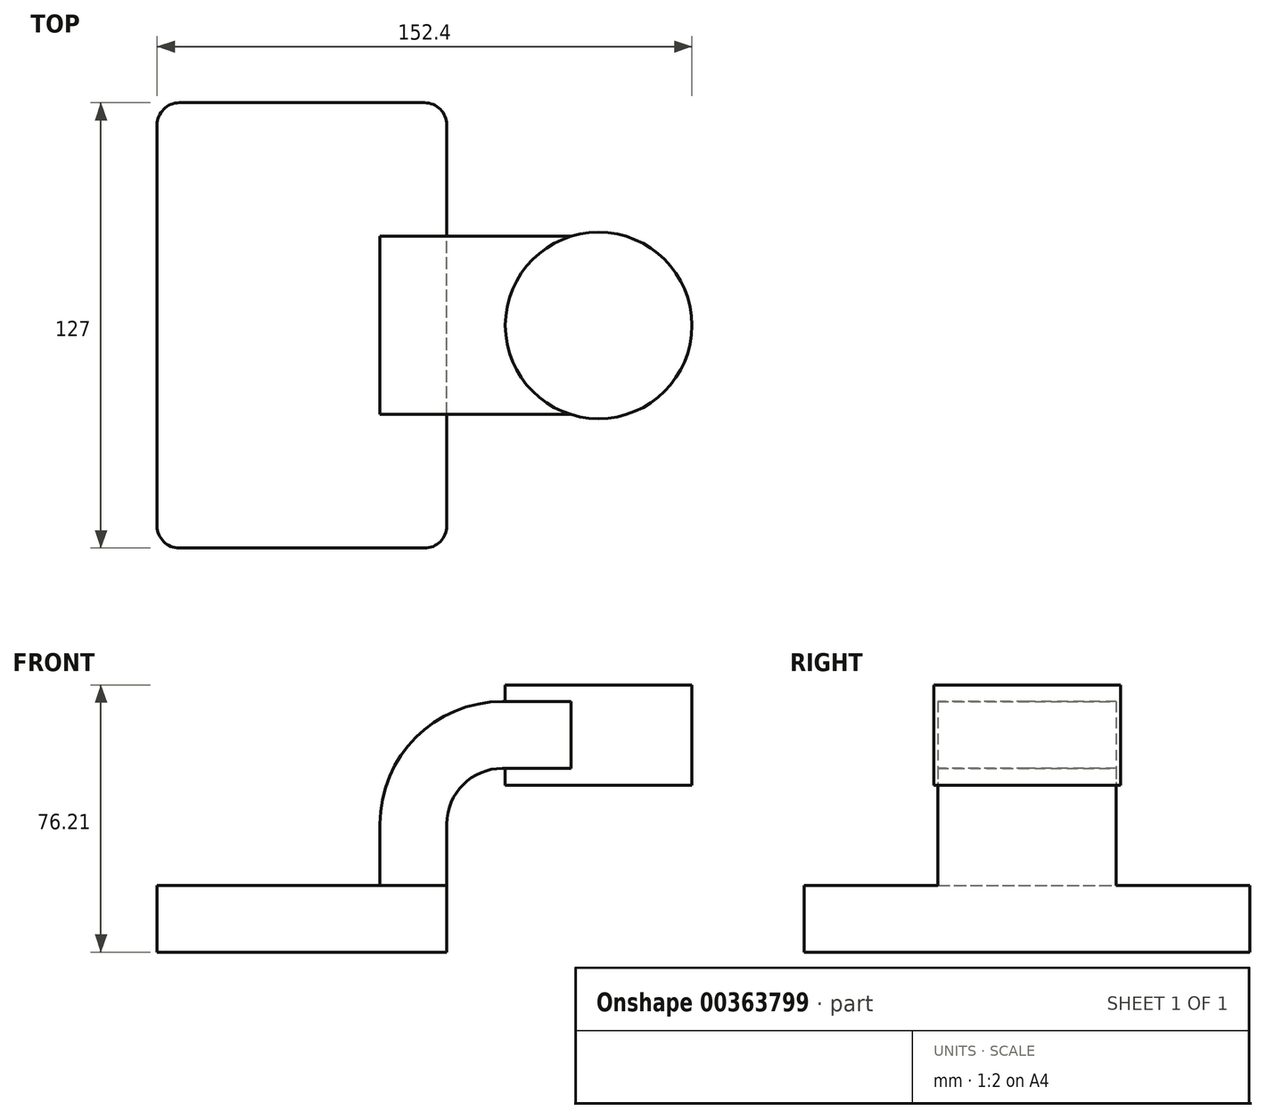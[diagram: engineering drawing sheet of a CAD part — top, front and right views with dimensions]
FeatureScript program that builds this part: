
annotation { "Feature Type Name" : "Feature", "Feature Type Description" : "" }
export const myFeature = defineFeature(function(context is Context, id is Id, definition is map)
    precondition{}
    {
        {
            var Q0;
            Q0=qCreatedBy(makeId("Front.planeOp"),FACE);
            var sketch = newSketch(context, id + "F0", { "sketchPlane" : qUnion([Q0])});
            skLineSegment(sketch, "E0.bottom", {"start": v(111.12, 66.68) * mm, "end": v(60.32, 66.68) * mm});
            skLineSegment(sketch, "E0.top", {"start": v(111.12, 38.1) * mm, "end": v(60.32, 38.1) * mm});
            skLineSegment(sketch, "E0.left", {"start": v(111.12, 66.68) * mm, "end": v(111.12, 38.1) * mm});
            skLineSegment(sketch, "E0.right", {"start": v(60.32, 66.68) * mm, "end": v(60.32, 38.1) * mm});
            skLineSegment(sketch, "E1", {"start": v(41.27, 9.53) * mm, "end": v(41.27, 27) * mm});
            skArc(sketch, "E2", {"start": v(41.27, 27) * mm, "mid": v(45.92, 38.23) * mm, "end": v(57.15, 42.88) * mm});
            skLineSegment(sketch, "E3", {"start": v(57.15, 42.88) * mm, "end": v(84.54, 42.88) * mm});
            skLineSegment(sketch, "E4.bottom", {"start": v(41.27, 9.53) * mm, "end": v(-41.28, 9.53) * mm});
            skLineSegment(sketch, "E4.top", {"start": v(41.28, -9.52) * mm, "end": v(-41.28, -9.53) * mm});
            skLineSegment(sketch, "E4.left", {"start": v(41.28, 9.53) * mm, "end": v(41.28, -9.52) * mm});
            skLineSegment(sketch, "E4.right", {"start": v(-41.28, 9.53) * mm, "end": v(-41.28, -9.53) * mm});
            skPoint(sketch, "E4.middle", {"position": v(0, 0) * mm});
            skLineSegment(sketch, "E5.0", {"start": v(57.15, 61.93) * mm, "end": v(84.54, 61.93) * mm});
            skArc(sketch, "E5.1", {"start": v(22.23, 27) * mm, "mid": v(32.45, 51.7) * mm, "end": v(57.15, 61.93) * mm});
            skLineSegment(sketch, "E5.2", {"start": v(22.22, 9.53) * mm, "end": v(22.22, 27) * mm});
            skLineSegment(sketch, "E6", {"start": v(84.54, 38.1) * mm, "end": v(84.54, 66.68) * mm});
            skFitSpline(sketch, "E7", {"points": [v(-41.28, 9.53) * mm, v(57.15, 61.93) * mm], "startDerivative": vector(-0.23, 58.1) * mm, "endDerivative": vector(111.91, -1.45) * mm});
            skSolve(sketch);
        }
        {
            var Q0;
            Q0=makeQuery(id+"F0.imprint","IMPRINT",FACE,{"disambiguationData":[TD([[makeQuery(id+"F0.imprint","IMPRINT",EDGE,{"derivedFrom":sQuery(id+"F0.wireOp",EDGE,"E4.top")}),-1.0]])]});
            extrude(context, id + "F1", {"entities" : qUnion([Q0]), "endBound" : BoundingType.SYMMETRIC, "depth" : 127 * mm});
        }
        {
            var Q0;
            {var subQ5=sQuery(id+"F0.wireOp",EDGE,"E1");Q0=makeQuery(id+"F0.imprint","IMPRINT",FACE,{"disambiguationData":[TD([[makeQuery(id+"F0.imprint","IMPRINT",EDGE,{"derivedFrom":subQ5}),1.0]])]});}
            var Q1;
            {var subQ0=sQuery(id+"F0.wireOp",EDGE,"E5.0");var subQ1=sQuery(id+"F0.wireOp",EDGE,"E0.right");var subQ2=makeQuery(id+"F0.imprint","INTERSECT",VERTEX,{"derivedFrom":[subQ1,subQ0]});Q1=makeQuery(id+"F0.imprint","IMPRINT",FACE,{"disambiguationData":[TD([[makeQuery(id+"F0.imprint","IMPRINT",EDGE,{"disambiguationData":[TD([[subQ2,-1.0]])],"derivedFrom":subQ1}),1.0]])]});}
            extrude(context, id + "F2", {"entities" : qUnion([Q0, Q1]), "operationType" : NewBodyOperationType.ADD, "endBound" : BoundingType.SYMMETRIC, "depth" : 50.8 * mm});
        }
        {
            var Q0;
            Q0=makeQuery(id+"F0.imprint","IMPRINT",FACE,{"disambiguationData":[TD([[makeQuery(id+"F0.imprint","IMPRINT",EDGE,{"derivedFrom":sQuery(id+"F0.wireOp",EDGE,"E5.1")}),1.0]])]});
            extrude(context, id + "F3", {"entities" : qUnion([Q0]), "operationType" : NewBodyOperationType.ADD, "endBound" : BoundingType.SYMMETRIC, "depth" : 15.88 * mm});
        }
        {
            var Q0;
            {var subQ4=sQuery(id+"F0.wireOp",EDGE,"E0.left");Q0=makeQuery(id+"F0.imprint","IMPRINT",FACE,{"disambiguationData":[TD([[makeQuery(id+"F0.imprint","IMPRINT",EDGE,{"derivedFrom":subQ4}),-1.0]])]});}
            var Q1;
            Q1=sQuery(id+"F0.wireOp",EDGE,"E6");
            revolve(context, id + "F4", {"operationType" : NewBodyOperationType.ADD, "entities" : qUnion([Q0]), "axis" : qUnion([Q1]), "revolveType" : RevolveType.FULL});
        }
        {
            var Q0;
            Q0=makeQuery(id+"F1.opExtrude","CAP_EDGE",EDGE,{"disambiguationData":[OSD([sQuery(id+"F0.wireOp",EDGE,"E4.right")])],"isStart":false});
            var Q1;
            Q1=makeQuery(id+"F1.opExtrude","CAP_EDGE",EDGE,{"disambiguationData":[OSD([sQuery(id+"F0.wireOp",EDGE,"E4.left")])],"isStart":false});
            var Q2;
            Q2=makeQuery(id+"F1.opExtrude","CAP_EDGE",EDGE,{"disambiguationData":[OSD([sQuery(id+"F0.wireOp",EDGE,"E4.left")])],"isStart":true});
            var Q3;
            Q3=makeQuery(id+"F1.opExtrude","CAP_EDGE",EDGE,{"disambiguationData":[OSD([sQuery(id+"F0.wireOp",EDGE,"E4.right")])],"isStart":true});
            fillet(context, id + "F5", {"entities" : qUnion([Q0, Q1, Q2, Q3]), "radius" : 6.35 * mm, "tangentPropagation" : true, "allowEdgeOverflow" : false});
        }
    });
